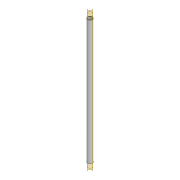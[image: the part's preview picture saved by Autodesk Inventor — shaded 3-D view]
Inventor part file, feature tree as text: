
AUTODESK INVENTOR PART (.ipt)
format: ipt  version: 2022 (Build 260153000, 153)  size: 76,800 bytes
history: native  units: mm
features: extrude x1, sketch x1
ambient origin geometry x8: Origin, YZ Plane, XZ Plane, XY Plane, X Axis, Y Axis, Z Axis, Center Point
bodies: Body1 (feature_tree)
feature tree (2):
  extrude  "Extrusion2"  Depth=300.0mm
  sketch  "Sketch2"  dims[d6=10.0mm d7=12.0mm d8=300.0mm d9=0.0mm]
